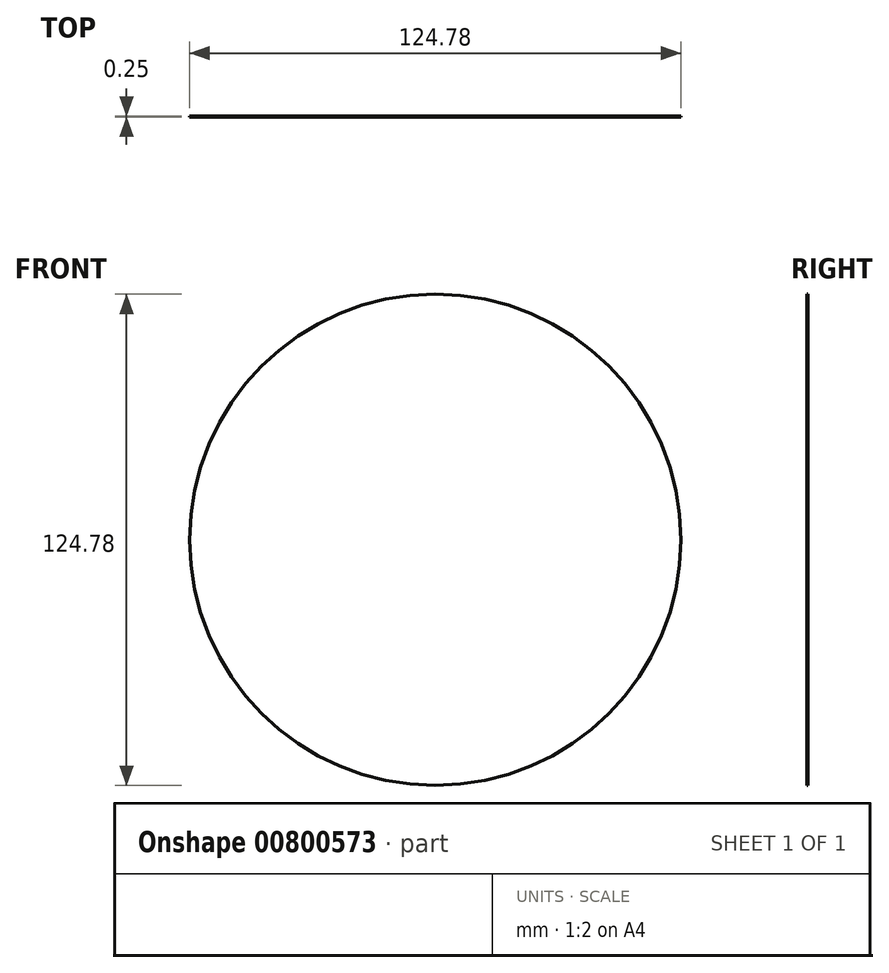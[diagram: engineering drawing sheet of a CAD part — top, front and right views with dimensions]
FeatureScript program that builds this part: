
annotation { "Feature Type Name" : "Feature", "Feature Type Description" : "" }
export const myFeature = defineFeature(function(context is Context, id is Id, definition is map)
    precondition{}
    {
        {
            var Q0;
            Q0=qCreatedBy(makeId("Front.planeOp"),FACE);
            var sketch = newSketch(context, id + "F0", { "sketchPlane" : qUnion([Q0])});
            skCircle(sketch, "E0", {"center": v(0, 0) * mm, "radius": 62.4 * mm});
            skSolve(sketch);
        }
        {
            var Q0;
            Q0=makeQuery(id+"F0.imprint","IMPRINT",FACE,{"disambiguationData":[TD([[makeQuery(id+"F0.imprint","IMPRINT",EDGE,{"derivedFrom":sQuery(id+"F0.wireOp",EDGE,"E0")}),1.0]])]});
            var Q1;
            Q1=sQuery(id+"F0.wireOp",EDGE,"E0");
            extrude(context, id + "F1", {"entities" : qUnion([Q0]), "surfaceEntities" : qUnion([Q1]), "depth" : 0.25 * mm, "offsetDistance" : 25.4 * mm});
        }
    });
